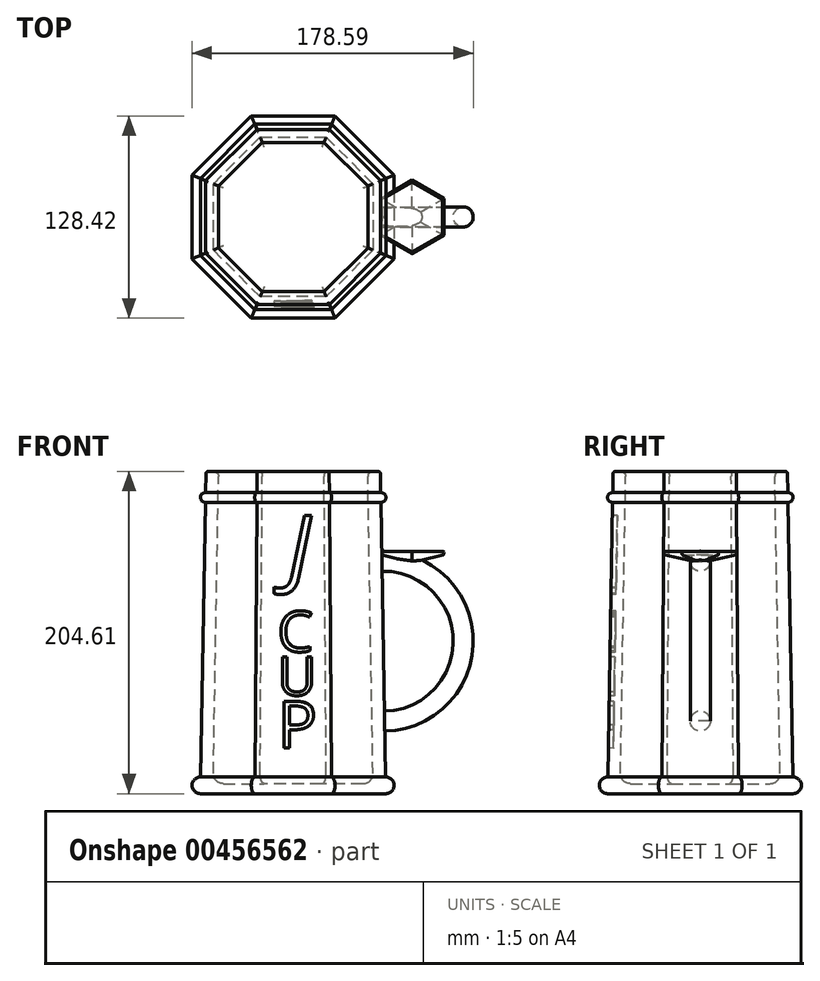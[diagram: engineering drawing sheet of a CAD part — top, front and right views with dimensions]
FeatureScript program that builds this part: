
annotation { "Feature Type Name" : "Feature", "Feature Type Description" : "" }
export const myFeature = defineFeature(function(context is Context, id is Id, definition is map)
    precondition{}
    {
        {
            var Q0;
            Q0=qCreatedBy(makeId("Front.planeOp"),FACE);
            var sketch = newSketch(context, id + "F0", { "sketchPlane" : qUnion([Q0])});
            skLineSegment(sketch, "E0", {"start": v(0, 0) * mm, "end": v(0, 270.51) * mm, "construction": true});
            skLineSegment(sketch, "E1", {"start": v(0, 0) * mm, "end": v(58.92, 0) * mm});
            skLineSegment(sketch, "E2", {"start": v(58.74, 10.58) * mm, "end": v(55.7, 185.03) * mm});
            skLineSegment(sketch, "E3", {"start": v(54.1, 204.6) * mm, "end": v(50.44, 204.6) * mm});
            skLineSegment(sketch, "E4", {"start": v(47.4, 201.5) * mm, "end": v(50.69, 12.81) * mm});
            skLineSegment(sketch, "E5", {"start": v(44.34, 6.35) * mm, "end": v(0, 6.35) * mm});
            skLineSegment(sketch, "E6", {"start": v(0, 6.35) * mm, "end": v(0, 0) * mm});
            skPoint(sketch, "E7.visualSharp", {"position": v(47.34, 204.6) * mm});
            skArc(sketch, "E7.filletArc", {"start": v(50.44, 204.6) * mm, "mid": v(48.27, 203.7) * mm, "end": v(47.4, 201.5) * mm});
            skPoint(sketch, "E8.visualSharp", {"position": v(55.35, 204.6) * mm});
            skArc(sketch, "E8.filletArc", {"start": v(55.37, 203.36) * mm, "mid": v(55, 204.24) * mm, "end": v(54.1, 204.6) * mm});
            skPoint(sketch, "E9.visualSharp", {"position": v(50.8, 6.35) * mm});
            skArc(sketch, "E9.filletArc", {"start": v(44.34, 6.35) * mm, "mid": v(48.87, 8.25) * mm, "end": v(50.69, 12.81) * mm});
            skArc(sketch, "E10", {"start": v(58.92, 0) * mm, "mid": v(64.21, 5.38) * mm, "end": v(58.74, 10.58) * mm});
            skArc(sketch, "E11", {"start": v(55.7, 185.03) * mm, "mid": v(58.9, 188.2) * mm, "end": v(55.59, 191.25) * mm});
            skLineSegment(sketch, "E12.trimOffspring", {"start": v(55.59, 191.25) * mm, "end": v(55.37, 203.36) * mm});
            skSolve(sketch);
        }
        {
            var Q0;
            Q0=qCreatedBy(makeId("Front.planeOp"),FACE);
            var sketch = newSketch(context, id + "F1", { "sketchPlane" : qUnion([Q0])});
            skArc(sketch, "E13", {"start": v(58.12, 46.06) * mm, "mid": v(108.03, 97.74) * mm, "end": v(56.35, 147.64) * mm});
            skSolve(sketch);
        }
        {
            var Q0;
            Q0=qCreatedBy(makeId("Right.planeOp"),FACE);
            var Q1;
            Q1=sQuery(id+"F1.wireOp",VERTEX,"E13.start");
            cPlane(context, id + "F2", {"entities" : qUnion([Q0, Q1]), "cplaneType" : CPlaneType.PLANE_POINT, "offset" : 25.4 * mm, "width" : 152.4 * mm, "height" : 152.4 * mm});
        }
        {
            var Q0;
            Q0=qCreatedBy(id+"F2.planeOp",FACE);
            var sketch = newSketch(context, id + "F3", { "sketchPlane" : qUnion([Q0])});
            skLineSegment(sketch, "E14.0", {"start": v(0, 46.06) * mm, "end": v(0, 147.65) * mm});
            skCircle(sketch, "E15", {"center": v(0, 46.06) * mm, "radius": 6.35 * mm});
            skSolve(sketch);
        }
        {
            var Q0;
            Q0=makeQuery(id+"F3.imprint","IMPRINT",FACE,{"disambiguationData":[TD([[makeQuery(id+"F3.imprint","IMPRINT",EDGE,{"derivedFrom":sQuery(id+"F3.wireOp",EDGE,"E15")}),1.0]])]});
            var Q1;
            Q1=sQuery(id+"F1.wireOp",EDGE,"E13");
            sweep(context, id + "F4", {"profiles" : qUnion([Q0]), "path" : qUnion([Q1])});
        }
        {
            var Q0;
            Q0=qCreatedBy(makeId("Top.planeOp"),FACE);
            var sketch = newSketch(context, id + "F5", { "sketchPlane" : qUnion([Q0])});
            skCircle(sketch, "E16.cCircle", {"center": v(0, 0) * mm, "radius": 58.69 * mm, "construction": true});
            skLineSegment(sketch, "E16.0", {"start": v(58.69, 24.3) * mm, "end": v(58.69, -24.3) * mm});
            skLineSegment(sketch, "E16.1", {"start": v(58.69, -24.3) * mm, "end": v(24.3, -58.69) * mm});
            skLineSegment(sketch, "E16.2", {"start": v(24.3, -58.69) * mm, "end": v(-24.3, -58.69) * mm});
            skLineSegment(sketch, "E16.3", {"start": v(-24.3, -58.69) * mm, "end": v(-58.69, -24.3) * mm});
            skLineSegment(sketch, "E16.4", {"start": v(-58.69, -24.3) * mm, "end": v(-58.69, 24.3) * mm});
            skLineSegment(sketch, "E16.5", {"start": v(-58.69, 24.3) * mm, "end": v(-24.3, 58.69) * mm});
            skLineSegment(sketch, "E16.6", {"start": v(-24.3, 58.69) * mm, "end": v(24.3, 58.69) * mm});
            skLineSegment(sketch, "E16.7", {"start": v(24.3, 58.69) * mm, "end": v(58.69, 24.3) * mm});
            skPoint(sketch, "E16.0.midPoint", {"position": v(58.69, 0) * mm});
            skSolve(sketch);
        }
        {
            var Q0;
            Q0=makeQuery(id+"F0.imprint","IMPRINT",FACE,{"disambiguationData":[TD([[makeQuery(id+"F0.imprint","IMPRINT",EDGE,{"derivedFrom":sQuery(id+"F0.wireOp",EDGE,"E1")}),1.0]])]});
            var Q1;
            Q1=sQuery(id+"F5.wireOp",EDGE,"E16.5");
            var Q2;
            Q2=sQuery(id+"F5.wireOp",EDGE,"E16.6");
            var Q3;
            Q3=sQuery(id+"F5.wireOp",EDGE,"E16.7");
            var Q4;
            Q4=sQuery(id+"F5.wireOp",EDGE,"E16.4");
            var Q5;
            Q5=sQuery(id+"F5.wireOp",EDGE,"E16.3");
            var Q6;
            Q6=sQuery(id+"F5.wireOp",EDGE,"E16.2");
            var Q7;
            Q7=sQuery(id+"F5.wireOp",EDGE,"E16.1");
            var Q8;
            Q8=sQuery(id+"F5.wireOp",EDGE,"E16.0");
            sweep(context, id + "F6", {"operationType" : NewBodyOperationType.ADD, "profiles" : qUnion([Q0]), "path" : qUnion([Q1, Q2, Q3, Q4, Q5, Q6, Q7, Q8])});
        }
        {
            var Q0;
            Q0=makeQuery(id+"F6.opSweep","SWEPT_FACE",FACE,{"disambiguationData":[OSD([sQuery(id+"F0.wireOp",EDGE,"E2"),sQuery(id+"F5.wireOp",EDGE,"E16.0")])]});
            var sketch = newSketch(context, id + "F7", { "sketchPlane" : qUnion([Q0])});
            skPoint(sketch, "E17", {"position": v(-0.89, 140.35) * mm});
            skSolve(sketch);
        }
        {
            var Q0;
            Q0=makeQuery(id+"F4.opSweep","CAP_EDGE",EDGE,{"disambiguationData":[OSD([sQuery(id+"F1.wireOp",VERTEX,"E13.end"),sQuery(id+"F3.wireOp",EDGE,"E15")])],"isStart":false});
            cPoint(context, id + "F8", {"entities" : qUnion([Q0]), "parameter" : 0.5});
        }
        {
            var Q0;
            Q0=qCreatedBy(makeId("Top.planeOp"),FACE);
            var Q1;
            Q1 = qCreatedBy(id + "F8" ,VERTEX);
            cPlane(context, id + "F9", {"entities" : qUnion([Q0, Q1]), "cplaneType" : CPlaneType.PLANE_POINT, "offset" : 25.4 * mm, "width" : 152.4 * mm, "height" : 152.4 * mm});
        }
        {
            var Q0;
            Q0=qCreatedBy(id+"F9.planeOp",FACE);
            var sketch = newSketch(context, id + "F10", { "sketchPlane" : qUnion([Q0])});
            skLineSegment(sketch, "E18", {"start": v(75.53, -14.23) * mm, "end": v(75.53, 13.54) * mm});
            skPoint(sketch, "E19.orphan", {"position": v(75.53, -26.22) * mm});
            skPoint(sketch, "E20.orphan", {"position": v(75.53, 26.22) * mm});
            skLineSegment(sketch, "E21.0.0", {"start": v(58.74, -24.33) * mm, "end": v(58.74, -24.33) * mm});
            skLineSegment(sketch, "E21.0.1", {"start": v(58.74, -24.33) * mm, "end": v(58.74, 24.33) * mm});
            skLineSegment(sketch, "E21.0.2", {"start": v(58.74, 24.33) * mm, "end": v(58.74, 24.33) * mm});
            skLineSegment(sketch, "E21.0.3", {"start": v(58.74, -24.33) * mm, "end": v(58.74, 24.33) * mm});
            skCircle(sketch, "E22.cCircle", {"center": v(75.53, 0) * mm, "radius": 16.8 * mm, "construction": true});
            skLineSegment(sketch, "E22.0", {"start": v(58.74, -9.7) * mm, "end": v(58.74, 9.7) * mm});
            skLineSegment(sketch, "E22.1", {"start": v(58.74, 9.7) * mm, "end": v(75.53, 19.4) * mm});
            skLineSegment(sketch, "E22.2", {"start": v(75.53, 19.4) * mm, "end": v(92.33, 9.7) * mm});
            skLineSegment(sketch, "E22.3", {"start": v(92.33, 9.7) * mm, "end": v(92.33, -9.7) * mm});
            skLineSegment(sketch, "E22.4", {"start": v(92.33, -9.7) * mm, "end": v(75.53, -19.4) * mm});
            skLineSegment(sketch, "E22.5", {"start": v(75.53, -19.4) * mm, "end": v(58.74, -9.7) * mm});
            skPoint(sketch, "E22.0.midPoint", {"position": v(58.74, 0) * mm});
            skSolve(sketch);
        }
        {
            var Q0;
            Q0=qCreatedBy(makeId("Front.planeOp"),FACE);
            var sketch = newSketch(context, id + "F11", { "sketchPlane" : qUnion([Q0])});
            skPoint(sketch, "E23.0", {"position": v(75.53, 154) * mm});
            skLineSegment(sketch, "E24.0.0", {"start": v(58.74, 10.58) * mm, "end": v(58.74, 10.58) * mm});
            skLineSegment(sketch, "E24.0.2", {"start": v(58.74, 10.58) * mm, "end": v(58.74, 10.58) * mm});
            skLineSegment(sketch, "E25", {"start": v(75.53, 154) * mm, "end": v(56.24, 154) * mm});
            skLineSegment(sketch, "E26", {"start": v(56.24, 154) * mm, "end": v(55.85, 153.99) * mm});
            skLineSegment(sketch, "E27", {"start": v(55.4, 153.44) * mm, "end": v(55.65, 151.98) * mm});
            skLineSegment(sketch, "E28", {"start": v(56, 151.6) * mm, "end": v(75.53, 146.63) * mm});
            skLineSegment(sketch, "E29", {"start": v(75.53, 146.63) * mm, "end": v(75.53, 154) * mm});
            skPoint(sketch, "E30.visualSharp", {"position": v(55.3, 153.98) * mm});
            skArc(sketch, "E30.filletArc", {"start": v(55.85, 153.99) * mm, "mid": v(55.5, 153.82) * mm, "end": v(55.4, 153.44) * mm});
            skPoint(sketch, "E31.visualSharp", {"position": v(55.7, 151.68) * mm});
            skArc(sketch, "E31.filletArc", {"start": v(55.65, 151.98) * mm, "mid": v(55.76, 151.74) * mm, "end": v(56, 151.6) * mm});
            skSolve(sketch);
        }
        {
            var Q0;
            Q0 = qSketchRegion(id + "F11", true);
            var Q1;
            Q1=sQuery(id+"F10.wireOp",EDGE,"E22.0");
            var Q2;
            Q2=sQuery(id+"F10.wireOp",EDGE,"E22.5");
            var Q3;
            Q3=sQuery(id+"F10.wireOp",EDGE,"E22.4");
            var Q4;
            Q4=sQuery(id+"F10.wireOp",EDGE,"E22.3");
            var Q5;
            Q5=sQuery(id+"F10.wireOp",EDGE,"E22.2");
            var Q6;
            Q6=sQuery(id+"F10.wireOp",EDGE,"E22.1");
            sweep(context, id + "F12", {"operationType" : NewBodyOperationType.ADD, "profiles" : qUnion([Q0]), "path" : qUnion([Q1, Q2, Q3, Q4, Q5, Q6])});
        }
        {
            var Q0;
            Q0=makeQuery(id+"F6.opSweep","SWEPT_FACE",FACE,{"disambiguationData":[OSD([sQuery(id+"F0.wireOp",EDGE,"E2"),sQuery(id+"F5.wireOp",EDGE,"E16.2")])]});
            var sketch = newSketch(context, id + "F13", { "sketchPlane" : qUnion([Q0])});
            skText(sketch, "E32", { "text": "J", "fontName": "OpenSans-Italic.ttf"});
            skText(sketch, "E33", { "text": "C", "fontName": "OpenSans-Regular.ttf"});
            skText(sketch, "E34", { "text": "U", "fontName": "OpenSans-Regular.ttf"});
            skText(sketch, "E35", { "text": "P", "fontName": "OpenSans-Regular.ttf"});
            const initialGuessF13  = {"E32": [-0.00355, 0.13597, 1, 0, 0.0401], "E33": [-0.01, 0.08916, 1, 0, 0.02589], "E34": [-0.00998, 0.06148, 1, 0, 0.02456], "E35": [-0.01, 0.02788, 1, 0, 0.02999]};
            skSetInitialGuess(sketch, initialGuessF13);
            skSolve(sketch);
        }
        {
            var Q0;
            Q0 = qSketchRegion(id + "F13", true);
            extrude(context, id + "F14", {"entities" : qUnion([Q0]), "operationType" : NewBodyOperationType.REMOVE, "oppositeDirection" : true, "depth" : 3.17 * mm});
        }
    });
